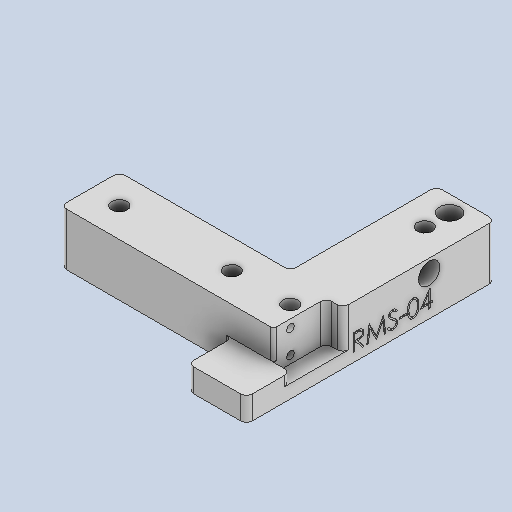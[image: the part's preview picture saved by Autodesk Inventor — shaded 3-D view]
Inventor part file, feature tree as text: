
AUTODESK INVENTOR PART (.ipt)
format: ipt  version: 2024.2 (Build 282272000, 272)  size: 248,832 bytes
history: native  units: in
note: dims shown in document units (in); Inventor stores cm internally (conversion verified against a paired STEP export)
features: fillet x1
ambient origin geometry x8: Origin, YZ Plane, XZ Plane, XY Plane, X Axis, Y Axis, Z Axis, Center Point
bodies: Solid1 (feature_tree)
feature tree (1):
  fillet  "Fillet3"  [1 undecoded]
note: 1 required parameter value undecoded (feature->parameter linkage not recoverable at this tier; creation-order binding heuristic only, values carry confidence <= 0.55)
